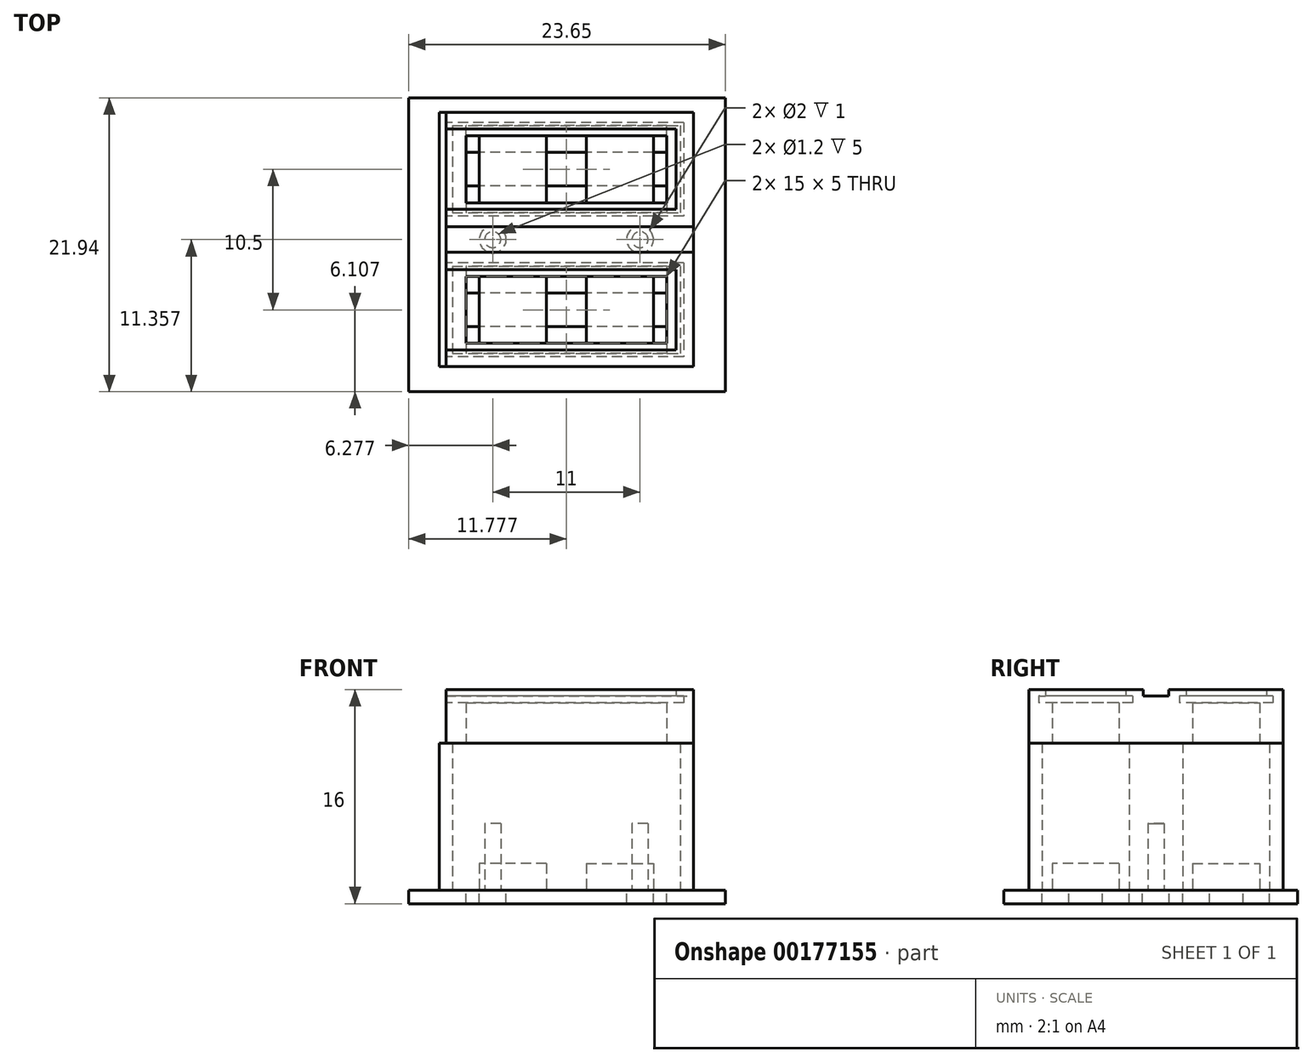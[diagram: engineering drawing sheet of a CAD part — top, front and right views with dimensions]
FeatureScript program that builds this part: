
annotation { "Feature Type Name" : "Feature", "Feature Type Description" : "" }
export const myFeature = defineFeature(function(context is Context, id is Id, definition is map)
    precondition{}
    {
        {
            var Q0;
            Q0=qCreatedBy(makeId("Top.planeOp"),FACE);
            var sketch = newSketch(context, id + "F0", { "sketchPlane" : qUnion([Q0])});
            skLineSegment(sketch, "E0.bottom", {"start": v(17.66, 9.32) * mm, "end": v(36.66, 9.32) * mm});
            skLineSegment(sketch, "E0.top", {"start": v(17.66, -9.68) * mm, "end": v(36.66, -9.68) * mm});
            skLineSegment(sketch, "E0.left", {"start": v(17.66, 9.32) * mm, "end": v(17.66, -9.68) * mm});
            skLineSegment(sketch, "E0.right", {"start": v(36.66, 9.32) * mm, "end": v(36.66, -9.68) * mm});
            skLineSegment(sketch, "E1.bottom", {"start": v(18.66, 8.32) * mm, "end": v(35.66, 8.32) * mm});
            skLineSegment(sketch, "E1.top", {"start": v(18.66, 1.82) * mm, "end": v(35.66, 1.82) * mm});
            skLineSegment(sketch, "E1.left", {"start": v(18.66, 8.32) * mm, "end": v(18.66, 1.82) * mm});
            skLineSegment(sketch, "E1.right", {"start": v(35.66, 8.32) * mm, "end": v(35.66, 1.82) * mm});
            skLineSegment(sketch, "E2.bottom", {"start": v(18.66, -2.18) * mm, "end": v(35.66, -2.18) * mm});
            skLineSegment(sketch, "E2.top", {"start": v(18.66, -8.68) * mm, "end": v(35.66, -8.68) * mm});
            skLineSegment(sketch, "E2.left", {"start": v(18.66, -2.18) * mm, "end": v(18.66, -8.68) * mm});
            skLineSegment(sketch, "E2.right", {"start": v(35.66, -2.18) * mm, "end": v(35.66, -8.68) * mm});
            skCircle(sketch, "E3", {"center": v(21.66, -0.18) * mm, "radius": 0.6 * mm, "construction": true});
            skCircle(sketch, "E4", {"center": v(32.66, -0.18) * mm, "radius": 0.6 * mm, "construction": true});
            skSolve(sketch);
        }
        {
            var Q0;
            Q0 = qSketchRegion(id + "F0", true);
            extrude(context, id + "F1", {"entities" : qUnion([Q0]), "depth" : 11 * mm});
        }
        {
            var Q0;
            Q0=qCreatedBy(makeId("Top.planeOp"),FACE);
            var sketch = newSketch(context, id + "F2", { "sketchPlane" : qUnion([Q0])});
            skLineSegment(sketch, "E5.bottom", {"start": v(25.66, 2.57) * mm, "end": v(20.66, 2.57) * mm});
            skLineSegment(sketch, "E5.top", {"start": v(25.66, 7.57) * mm, "end": v(20.66, 7.57) * mm});
            skLineSegment(sketch, "E5.left", {"start": v(25.66, 2.57) * mm, "end": v(25.66, 7.57) * mm});
            skLineSegment(sketch, "E5.right", {"start": v(20.66, 2.57) * mm, "end": v(20.66, 7.57) * mm});
            skPoint(sketch, "E5.middle", {"position": v(23.16, 5.07) * mm});
            skLineSegment(sketch, "E6.bottom", {"start": v(25.66, -2.93) * mm, "end": v(20.66, -2.93) * mm});
            skLineSegment(sketch, "E6.top", {"start": v(25.66, -7.93) * mm, "end": v(20.66, -7.93) * mm});
            skLineSegment(sketch, "E6.left", {"start": v(25.66, -2.93) * mm, "end": v(25.66, -7.93) * mm});
            skLineSegment(sketch, "E6.right", {"start": v(20.66, -2.93) * mm, "end": v(20.66, -7.93) * mm});
            skPoint(sketch, "E6.middle", {"position": v(23.16, -5.43) * mm});
            skLineSegment(sketch, "E7.bottom", {"start": v(28.66, 2.57) * mm, "end": v(33.66, 2.57) * mm});
            skLineSegment(sketch, "E7.top", {"start": v(28.66, 7.57) * mm, "end": v(33.66, 7.57) * mm});
            skLineSegment(sketch, "E7.left", {"start": v(28.66, 2.57) * mm, "end": v(28.66, 7.57) * mm});
            skLineSegment(sketch, "E7.right", {"start": v(33.66, 2.57) * mm, "end": v(33.66, 7.57) * mm});
            skPoint(sketch, "E7.middle", {"position": v(31.16, 5.07) * mm});
            skLineSegment(sketch, "E8.bottom", {"start": v(28.66, -7.93) * mm, "end": v(33.66, -7.93) * mm});
            skLineSegment(sketch, "E8.top", {"start": v(28.66, -2.93) * mm, "end": v(33.66, -2.93) * mm});
            skLineSegment(sketch, "E8.left", {"start": v(28.66, -7.93) * mm, "end": v(28.66, -2.93) * mm});
            skLineSegment(sketch, "E8.right", {"start": v(33.66, -7.93) * mm, "end": v(33.66, -2.93) * mm});
            skPoint(sketch, "E8.middle", {"position": v(31.16, -5.43) * mm});
            skSolve(sketch);
        }
        {
            var Q0;
            Q0 = qSketchRegion(id + "F2", true);
            extrude(context, id + "F3", {"entities" : qUnion([Q0]), "depth" : 2 * mm});
        }
        {
            var Q0;
            Q0=makeQuery(id+"F1.opExtrude","CAP_FACE",FACE,{"disambiguationData":[OSD([sQuery(id+"F0.wireOp",EDGE,"E0.bottom"),sQuery(id+"F0.wireOp",EDGE,"E0.top"),sQuery(id+"F0.wireOp",EDGE,"E0.left"),sQuery(id+"F0.wireOp",EDGE,"E0.right"),sQuery(id+"F0.wireOp",EDGE,"E1.bottom"),sQuery(id+"F0.wireOp",EDGE,"E1.top"),sQuery(id+"F0.wireOp",EDGE,"E1.left"),sQuery(id+"F0.wireOp",EDGE,"E1.right"),sQuery(id+"F0.wireOp",EDGE,"E2.bottom"),sQuery(id+"F0.wireOp",EDGE,"E2.top"),sQuery(id+"F0.wireOp",EDGE,"E2.left"),sQuery(id+"F0.wireOp",EDGE,"E2.right"),sQuery(id+"F0.wireOp",EDGE,"E3"),sQuery(id+"F0.wireOp",EDGE,"E4")])],"isStart":false});
            var sketch = newSketch(context, id + "F4", { "sketchPlane" : qUnion([Q0])});
            skLineSegment(sketch, "E9.bottom", {"start": v(18.16, 9.32) * mm, "end": v(36.66, 9.32) * mm});
            skLineSegment(sketch, "E9.top", {"start": v(18.16, -9.68) * mm, "end": v(36.66, -9.68) * mm});
            skLineSegment(sketch, "E9.left", {"start": v(18.16, 9.32) * mm, "end": v(18.16, -9.68) * mm});
            skLineSegment(sketch, "E9.right", {"start": v(36.66, 9.32) * mm, "end": v(36.66, -9.68) * mm});
            skLineSegment(sketch, "E10.bottom", {"start": v(19.66, -2.93) * mm, "end": v(34.66, -2.93) * mm});
            skLineSegment(sketch, "E10.top", {"start": v(19.66, -7.93) * mm, "end": v(34.66, -7.93) * mm});
            skLineSegment(sketch, "E10.left", {"start": v(19.66, -2.93) * mm, "end": v(19.66, -7.93) * mm});
            skLineSegment(sketch, "E10.right", {"start": v(34.66, -2.93) * mm, "end": v(34.66, -7.93) * mm});
            skLineSegment(sketch, "E11.bottom", {"start": v(19.66, 2.57) * mm, "end": v(34.66, 2.57) * mm});
            skLineSegment(sketch, "E11.top", {"start": v(19.66, 7.57) * mm, "end": v(34.66, 7.57) * mm});
            skLineSegment(sketch, "E11.left", {"start": v(19.66, 2.57) * mm, "end": v(19.66, 7.57) * mm});
            skLineSegment(sketch, "E11.right", {"start": v(34.66, 2.57) * mm, "end": v(34.66, 7.57) * mm});
            skSolve(sketch);
        }
        {
            var Q0;
            Q0 = qSketchRegion(id + "F4", true);
            extrude(context, id + "F5", {"entities" : qUnion([Q0]), "depth" : 3 * mm});
        }
        {
            var Q0;
            Q0=makeQuery(id+"F5.opExtrude","CAP_FACE",FACE,{"disambiguationData":[OSD([sQuery(id+"F4.wireOp",EDGE,"E9.bottom"),sQuery(id+"F4.wireOp",EDGE,"E9.top"),sQuery(id+"F4.wireOp",EDGE,"E9.left"),sQuery(id+"F4.wireOp",EDGE,"E9.right"),sQuery(id+"F4.wireOp",EDGE,"E10.bottom"),sQuery(id+"F4.wireOp",EDGE,"E10.top"),sQuery(id+"F4.wireOp",EDGE,"E10.left"),sQuery(id+"F4.wireOp",EDGE,"E10.right"),sQuery(id+"F4.wireOp",EDGE,"E11.bottom"),sQuery(id+"F4.wireOp",EDGE,"E11.top"),sQuery(id+"F4.wireOp",EDGE,"E11.left"),sQuery(id+"F4.wireOp",EDGE,"E11.right")])],"isStart":false});
            var sketch = newSketch(context, id + "F6", { "sketchPlane" : qUnion([Q0])});
            skLineSegment(sketch, "E12.bottom", {"start": v(36.66, 9.32) * mm, "end": v(35.9, 9.32) * mm});
            skLineSegment(sketch, "E12.top", {"start": v(36.66, -9.68) * mm, "end": v(35.9, -9.68) * mm});
            skLineSegment(sketch, "E12.left", {"start": v(36.66, 9.32) * mm, "end": v(36.66, -9.68) * mm});
            skLineSegment(sketch, "E12.right", {"start": v(35.9, 9.32) * mm, "end": v(35.9, -9.68) * mm});
            skLineSegment(sketch, "E13.bottom", {"start": v(35.9, 9.32) * mm, "end": v(18.16, 9.32) * mm});
            skLineSegment(sketch, "E13.top", {"start": v(35.9, 8.57) * mm, "end": v(18.16, 8.57) * mm});
            skLineSegment(sketch, "E13.left", {"start": v(35.9, 9.32) * mm, "end": v(35.9, 8.57) * mm});
            skLineSegment(sketch, "E13.right", {"start": v(18.16, 9.32) * mm, "end": v(18.16, 8.57) * mm});
            skLineSegment(sketch, "E14.bottom", {"start": v(35.9, -9.68) * mm, "end": v(18.16, -9.68) * mm});
            skLineSegment(sketch, "E14.top", {"start": v(35.9, -8.93) * mm, "end": v(18.16, -8.93) * mm});
            skLineSegment(sketch, "E14.left", {"start": v(35.9, -9.68) * mm, "end": v(35.9, -8.93) * mm});
            skLineSegment(sketch, "E14.right", {"start": v(18.16, -9.68) * mm, "end": v(18.16, -8.93) * mm});
            skLineSegment(sketch, "E15.bottom", {"start": v(35.9, 1.57) * mm, "end": v(18.16, 1.57) * mm});
            skLineSegment(sketch, "E15.top", {"start": v(35.9, -1.93) * mm, "end": v(18.16, -1.93) * mm});
            skLineSegment(sketch, "E15.left", {"start": v(35.9, 1.57) * mm, "end": v(35.9, -1.93) * mm});
            skLineSegment(sketch, "E15.right", {"start": v(18.16, 1.57) * mm, "end": v(18.16, -1.93) * mm});
            skSolve(sketch);
        }
        {
            var Q0;
            Q0 = qSketchRegion(id + "F6", true);
            extrude(context, id + "F7", {"entities" : qUnion([Q0]), "operationType" : NewBodyOperationType.ADD, "depth" : 0.5 * mm});
        }
        {
            var Q0;
            Q0=makeQuery(id+"F7.opExtrude","CAP_FACE",FACE,{"disambiguationData":[OSD([sQuery(id+"F6.wireOp",EDGE,"E12.bottom"),sQuery(id+"F6.wireOp",EDGE,"E12.top"),sQuery(id+"F6.wireOp",EDGE,"E12.left"),sQuery(id+"F6.wireOp",EDGE,"E12.right"),sQuery(id+"F6.wireOp",EDGE,"E13.bottom"),sQuery(id+"F6.wireOp",EDGE,"E13.top"),sQuery(id+"F6.wireOp",EDGE,"E13.right"),sQuery(id+"F6.wireOp",EDGE,"E14.bottom"),sQuery(id+"F6.wireOp",EDGE,"E14.top"),sQuery(id+"F6.wireOp",EDGE,"E14.right"),sQuery(id+"F6.wireOp",EDGE,"E15.bottom"),sQuery(id+"F6.wireOp",EDGE,"E15.top"),sQuery(id+"F6.wireOp",EDGE,"E15.right")])],"isStart":false});
            var sketch = newSketch(context, id + "F8", { "sketchPlane" : qUnion([Q0])});
            skLineSegment(sketch, "E16.bottom", {"start": v(36.66, 9.32) * mm, "end": v(35.36, 9.32) * mm});
            skLineSegment(sketch, "E16.top", {"start": v(36.66, -9.68) * mm, "end": v(35.36, -9.68) * mm});
            skLineSegment(sketch, "E16.left", {"start": v(36.66, 9.32) * mm, "end": v(36.66, -9.68) * mm});
            skLineSegment(sketch, "E16.right", {"start": v(35.36, 9.32) * mm, "end": v(35.36, -9.68) * mm});
            skLineSegment(sketch, "E17.bottom", {"start": v(18.16, 9.32) * mm, "end": v(35.36, 9.32) * mm});
            skLineSegment(sketch, "E17.top", {"start": v(18.16, 8.07) * mm, "end": v(35.36, 8.07) * mm});
            skLineSegment(sketch, "E17.left", {"start": v(18.16, 9.32) * mm, "end": v(18.16, 8.07) * mm});
            skLineSegment(sketch, "E17.right", {"start": v(35.36, 9.32) * mm, "end": v(35.36, 8.07) * mm});
            skLineSegment(sketch, "E18.bottom", {"start": v(18.16, -9.68) * mm, "end": v(35.36, -9.68) * mm});
            skLineSegment(sketch, "E18.top", {"start": v(18.16, -8.43) * mm, "end": v(35.36, -8.43) * mm});
            skLineSegment(sketch, "E18.left", {"start": v(18.16, -9.68) * mm, "end": v(18.16, -8.43) * mm});
            skLineSegment(sketch, "E18.right", {"start": v(35.36, -9.68) * mm, "end": v(35.36, -8.43) * mm});
            skLineSegment(sketch, "E19.bottom", {"start": v(35.36, 2.07) * mm, "end": v(18.16, 2.07) * mm});
            skLineSegment(sketch, "E19.top", {"start": v(35.36, -2.43) * mm, "end": v(18.16, -2.43) * mm});
            skLineSegment(sketch, "E19.left", {"start": v(35.36, 2.07) * mm, "end": v(35.36, -2.43) * mm});
            skLineSegment(sketch, "E19.right", {"start": v(18.16, 2.07) * mm, "end": v(18.16, -2.43) * mm});
            skSolve(sketch);
        }
        {
            var Q0;
            Q0 = qSketchRegion(id + "F8", true);
            extrude(context, id + "F9", {"entities" : qUnion([Q0]), "operationType" : NewBodyOperationType.ADD, "depth" : 0.5 * mm});
        }
        {
            var Q0;
            Q0=makeQuery(id+"F9.opExtrude","CAP_FACE",FACE,{"disambiguationData":[OSD([sQuery(id+"F8.wireOp",EDGE,"E16.bottom"),sQuery(id+"F8.wireOp",EDGE,"E16.top"),sQuery(id+"F8.wireOp",EDGE,"E16.left"),sQuery(id+"F8.wireOp",EDGE,"E16.right"),sQuery(id+"F8.wireOp",EDGE,"E17.bottom"),sQuery(id+"F8.wireOp",EDGE,"E17.top"),sQuery(id+"F8.wireOp",EDGE,"E17.left"),sQuery(id+"F8.wireOp",EDGE,"E18.bottom"),sQuery(id+"F8.wireOp",EDGE,"E18.top"),sQuery(id+"F8.wireOp",EDGE,"E18.left"),sQuery(id+"F8.wireOp",EDGE,"E19.bottom"),sQuery(id+"F8.wireOp",EDGE,"E19.top"),sQuery(id+"F8.wireOp",EDGE,"E19.right")])],"isStart":false});
            var sketch = newSketch(context, id + "F10", { "sketchPlane" : qUnion([Q0])});
            skLineSegment(sketch, "E20.bottom", {"start": v(18.16, 0.77) * mm, "end": v(36.66, 0.77) * mm});
            skLineSegment(sketch, "E20.top", {"start": v(18.16, -1.13) * mm, "end": v(36.66, -1.13) * mm});
            skLineSegment(sketch, "E20.left", {"start": v(18.16, 0.77) * mm, "end": v(18.16, -1.13) * mm});
            skLineSegment(sketch, "E20.right", {"start": v(36.66, 0.77) * mm, "end": v(36.66, -1.13) * mm});
            skSolve(sketch);
        }
        {
            var Q0;
            Q0 = qSketchRegion(id + "F10", true);
            extrude(context, id + "F11", {"entities" : qUnion([Q0]), "operationType" : NewBodyOperationType.REMOVE, "oppositeDirection" : true, "depth" : 0.5 * mm});
        }
        {
            var Q0;
            Q0=qCreatedBy(makeId("Top.planeOp"),FACE);
            var sketch = newSketch(context, id + "F12", { "sketchPlane" : qUnion([Q0])});
            skLineSegment(sketch, "E21.bottom", {"start": v(15.38, 10.4) * mm, "end": v(39.03, 10.4) * mm});
            skLineSegment(sketch, "E21.top", {"start": v(15.38, -11.54) * mm, "end": v(39.03, -11.54) * mm});
            skLineSegment(sketch, "E21.left", {"start": v(15.38, 10.4) * mm, "end": v(15.38, -11.54) * mm});
            skLineSegment(sketch, "E21.right", {"start": v(39.03, 10.4) * mm, "end": v(39.03, -11.54) * mm});
            skCircle(sketch, "E22", {"center": v(21.66, -0.18) * mm, "radius": 1 * mm});
            skCircle(sketch, "E23", {"center": v(32.66, -0.18) * mm, "radius": 1 * mm});
            skPoint(sketch, "E24", {"position": v(27.16, -0.18) * mm});
            skLineSegment(sketch, "E25.bottom", {"start": v(34.66, 6.32) * mm, "end": v(19.66, 6.32) * mm});
            skLineSegment(sketch, "E25.top", {"start": v(34.66, 8.32) * mm, "end": v(19.66, 8.32) * mm});
            skLineSegment(sketch, "E25.left", {"start": v(34.66, 6.32) * mm, "end": v(34.66, 8.32) * mm});
            skLineSegment(sketch, "E25.right", {"start": v(19.66, 6.32) * mm, "end": v(19.66, 8.32) * mm});
            skPoint(sketch, "E25.middle", {"position": v(27.16, 7.32) * mm});
            skLineSegment(sketch, "E26.bottom", {"start": v(34.66, 3.82) * mm, "end": v(19.66, 3.82) * mm});
            skLineSegment(sketch, "E26.top", {"start": v(34.66, 1.82) * mm, "end": v(19.66, 1.82) * mm});
            skLineSegment(sketch, "E26.left", {"start": v(34.66, 3.82) * mm, "end": v(34.66, 1.82) * mm});
            skLineSegment(sketch, "E26.right", {"start": v(19.66, 3.82) * mm, "end": v(19.66, 1.82) * mm});
            skPoint(sketch, "E26.middle", {"position": v(27.16, 2.82) * mm});
            skLineSegment(sketch, "E27.bottom", {"start": v(34.66, -2.18) * mm, "end": v(19.66, -2.18) * mm});
            skLineSegment(sketch, "E27.top", {"start": v(34.66, -4.18) * mm, "end": v(19.66, -4.18) * mm});
            skLineSegment(sketch, "E27.left", {"start": v(34.66, -2.18) * mm, "end": v(34.66, -4.18) * mm});
            skLineSegment(sketch, "E27.right", {"start": v(19.66, -2.18) * mm, "end": v(19.66, -4.18) * mm});
            skPoint(sketch, "E27.middle", {"position": v(27.16, -3.18) * mm});
            skLineSegment(sketch, "E28.bottom", {"start": v(34.66, -6.68) * mm, "end": v(19.66, -6.68) * mm});
            skLineSegment(sketch, "E28.top", {"start": v(34.66, -8.68) * mm, "end": v(19.66, -8.68) * mm});
            skLineSegment(sketch, "E28.left", {"start": v(34.66, -6.68) * mm, "end": v(34.66, -8.68) * mm});
            skLineSegment(sketch, "E28.right", {"start": v(19.66, -6.68) * mm, "end": v(19.66, -8.68) * mm});
            skPoint(sketch, "E28.middle", {"position": v(27.16, -7.68) * mm});
            skSolve(sketch);
        }
        {
            var Q0;
            Q0 = qSketchRegion(id + "F12", true);
            extrude(context, id + "F13", {"entities" : qUnion([Q0]), "oppositeDirection" : true, "depth" : 1 * mm});
        }
        {
            var Q0;
            Q0=makeQuery(id+"F13.opExtrude","CAP_FACE",FACE,{"disambiguationData":[OSD([sQuery(id+"F12.wireOp",EDGE,"E21.bottom"),sQuery(id+"F12.wireOp",EDGE,"E21.top"),sQuery(id+"F12.wireOp",EDGE,"E21.left"),sQuery(id+"F12.wireOp",EDGE,"E21.right")])],"isStart":true});
            var sketch = newSketch(context, id + "F14", { "sketchPlane" : qUnion([Q0])});
            skLineSegment(sketch, "E29.bottom", {"start": v(29.1, -2.18) * mm, "end": v(25.2, -2.18) * mm});
            skLineSegment(sketch, "E29.top", {"start": v(29.1, 1.82) * mm, "end": v(25.2, 1.82) * mm});
            skLineSegment(sketch, "E29.left", {"start": v(29.1, -2.18) * mm, "end": v(29.1, 1.82) * mm});
            skLineSegment(sketch, "E29.right", {"start": v(25.2, -2.18) * mm, "end": v(25.2, 1.82) * mm});
            skPoint(sketch, "E29.middle", {"position": v(27.16, -0.18) * mm});
            skSolve(sketch);
        }
        {
            var Q0;
            Q0 = qSketchRegion(id + "F14", true);
            extrude(context, id + "F15", {"entities" : qUnion([Q0]), "operationType" : NewBodyOperationType.ADD, "depth" : 2.9 * mm});
        }
        {
            var Q0;
            Q0=makeQuery(id+"F0.imprint","IMPRINT",FACE,{"disambiguationData":[TD([[makeQuery(id+"F0.imprint","IMPRINT",EDGE,{"derivedFrom":sQuery(id+"F0.wireOp",EDGE,"E0.bottom")}),-1.0]])]});
            var sketch = newSketch(context, id + "F16", { "sketchPlane" : qUnion([Q0])});
            skCircle(sketch, "E30", {"center": v(21.66, -0.18) * mm, "radius": 0.6 * mm});
            skCircle(sketch, "E31", {"center": v(32.66, -0.18) * mm, "radius": 0.6 * mm});
            skSolve(sketch);
        }
        {
            var Q0;
            Q0 = qSketchRegion(id + "F16", true);
            extrude(context, id + "F17", {"entities" : qUnion([Q0]), "operationType" : NewBodyOperationType.REMOVE, "depth" : 5 * mm});
        }
    });
